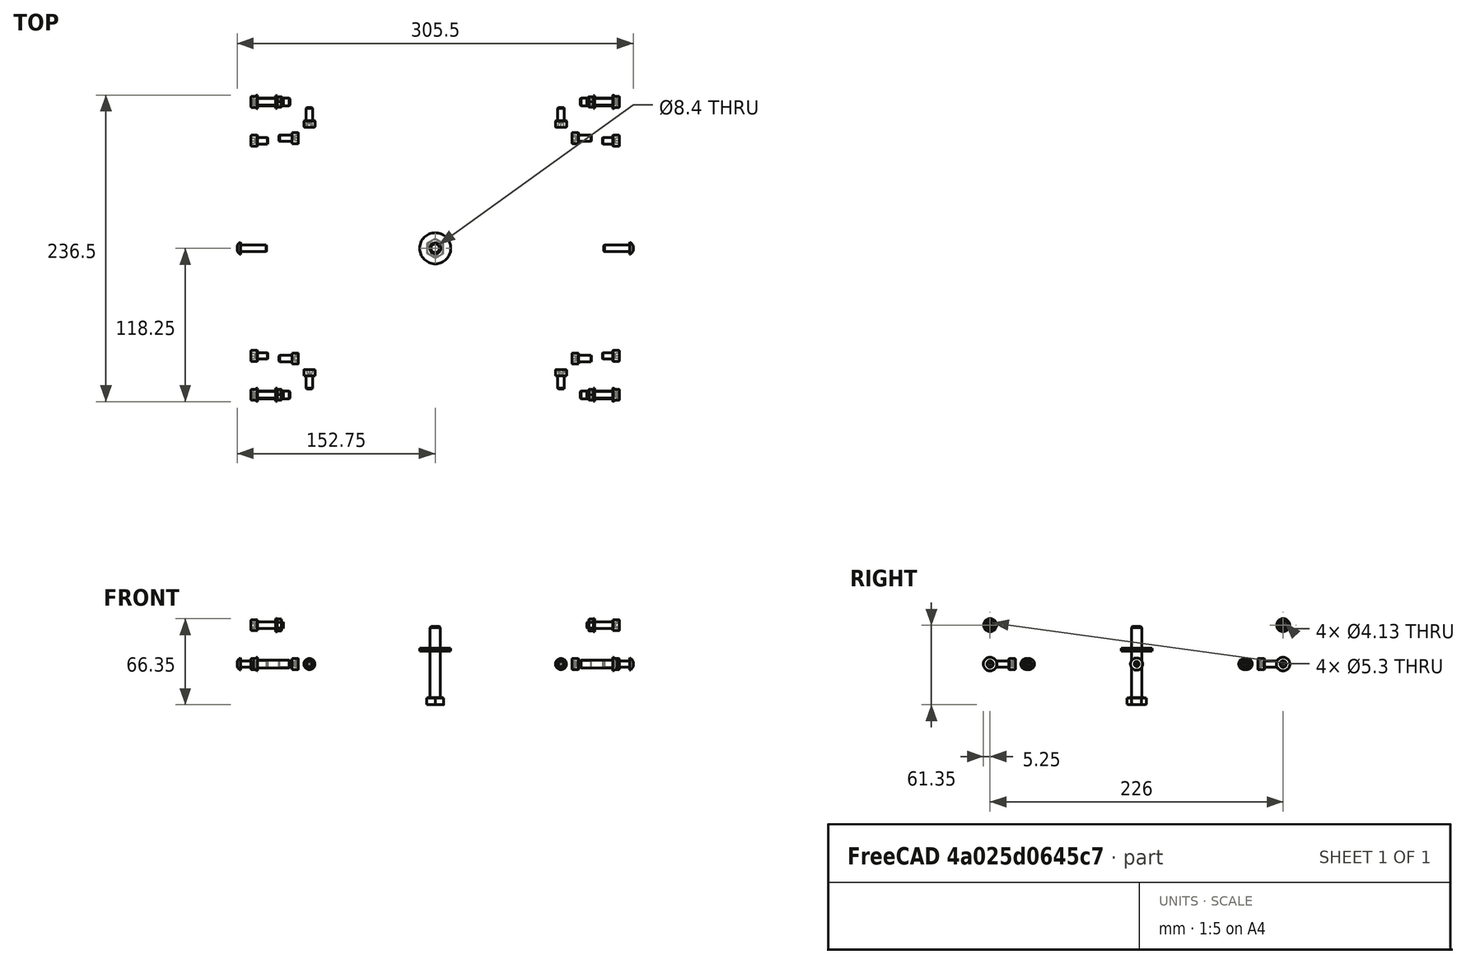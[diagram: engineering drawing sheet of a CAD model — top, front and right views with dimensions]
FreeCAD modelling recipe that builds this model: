
FCSTD DOCUMENT  (FreeCAD 0.19R24276 (Git))
Label: v5.6_Base
License: All rights reserved
LicenseURL: http://en.wikipedia.org/wiki/All_rights_reserved
objects: App::Link×37, Part::FeaturePython×32, App::DocumentObjectGroup×2, PartDesign::CoordinateSystem×2, App::FeaturePython×1, App::Part×1
note: 34 computed .brp shape members not serialized (recipe doc carries the construction recipe); baked Part::Feature solids carry a one-line shape summary decoded from their .brp
EXTERNAL_REF file=v5.6_Master.FCStd obj=LCS_AFrame_BaseHub
EXTERNAL_REF file=v5.6_Master.FCStd obj=Part002
EXTERNAL_REF file=v5.6_Master.FCStd obj=LCS_AFrame_Corner_AP
EXTERNAL_REF file=v5.6_Master.FCStd obj=Local_CS097
EXTERNAL_REF file=v5.6_Master.FCStd obj=Body038
EXTERNAL_REF file=v5.6_Master.FCStd obj=LCS_AFrame_Corner_FP
EXTERNAL_REF file=v5.6_Master.FCStd obj=LCS_AFrame_Corner_AS
EXTERNAL_REF file=v5.6_Master.FCStd obj=LCS_AFrame_Corner_FS
EXTERNAL_REF file=v5.6_Master.FCStd obj=LCS_AFrame_Post_AP
EXTERNAL_REF file=v5.6_Master.FCStd obj=Local_CS042
EXTERNAL_REF file=v5.6_Master.FCStd obj=Body018
EXTERNAL_REF file=v5.6_Master.FCStd obj=LCS_AFrame_Post_FP
EXTERNAL_REF file=v5.6_Master.FCStd obj=Local_CS044
EXTERNAL_REF file=v5.6_Master.FCStd obj=LCS_AFrame_Post_AS
EXTERNAL_REF file=v5.6_Master.FCStd obj=LCS_AFrame_Post_FS
EXTERNAL_REF file=v5.6_Master.FCStd obj=Local_CS208
EXTERNAL_REF file=v5.6_Master.FCStd obj=Body022020
EXTERNAL_REF file=v5.6_Master.FCStd obj=Local_CS061
EXTERNAL_REF file=v5.6_Master.FCStd obj=Body020
EXTERNAL_REF file=v5.6_Master.FCStd obj=Local_CS059
EXTERNAL_REF file=v5.6_Master.FCStd obj=Local_CS212
EXTERNAL_REF file=v5.6_Master.FCStd obj=Local_CS217
EXTERNAL_REF file=v5.6_Master.FCStd obj=Body022016
EXTERNAL_REF file=v5.6_Master.FCStd obj=Local_CS213
EXTERNAL_REF file=v5.6_Master.FCStd obj=Local_CS215
EXTERNAL_REF file=v5.6_Master.FCStd obj=Body022017
EXTERNAL_REF file=v5.6_Master.FCStd obj=Local_CS214
EXTERNAL_REF file=v5.6_Master.FCStd obj=Local_CS216
EXTERNAL_REF file=v5.6_Master.FCStd obj=Body022022
EXTERNAL_REF file=v5.6_Master.FCStd obj=Local_CS100
EXTERNAL_REF file=v5.6_Master.FCStd obj=Local_CS108
EXTERNAL_REF file=v5.6_Master.FCStd obj=Body039
EXTERNAL_REF file=v5.6_Master.FCStd obj=Local_CS109
EXTERNAL_REF file=v5.6_Master.FCStd obj=Local_CS111
EXTERNAL_REF file=v5.6_Master.FCStd obj=Local_CS113
EXTERNAL_REF file=v5.6_Master.FCStd obj=Local_CS110
EXTERNAL_REF file=v5.6_Master.FCStd obj=Local_CS112
EXTERNAL_REF file=v5.6_Master.FCStd obj=Local_CS207
EXTERNAL_REF file=v5.6_Master.FCStd obj=Local_CS098
EXTERNAL_REF file=v5.6_Master.FCStd obj=Local_CS099
EXTERNAL_REF file=v5.6_Master.FCStd obj=Local_CS063
EXTERNAL_REF file=v5.6_Master.FCStd obj=Local_CS065
EXTERNAL_REF file=v5.6_Master.FCStd obj=Local_CS182
EXTERNAL_REF file=v5.6_Master.FCStd obj=Local_CS184
EXTERNAL_REF file=v5.6_Master.FCStd obj=Local_CS183
EXTERNAL_REF file=v5.6_Master.FCStd obj=Local_CS185
EXTERNAL_REF file=v5.6_Master.FCStd obj=Local_CS189
EXTERNAL_REF file=v5.6_Master.FCStd obj=Local_CS190
EXTERNAL_REF file=v5.6_Master.FCStd obj=LCS_AFrame_Pivot
EXTERNAL_REF file=v5.6_Master.FCStd obj=Local_CS233
EXTERNAL_REF file=v5.6_Master.FCStd obj=Body022031
EXTERNAL_REF file=v5.6_Master.FCStd obj=Local_CS236
EXTERNAL_REF file=v5.6_Master.FCStd obj=Body003

FEATURE [App::DocumentObjectGroup] Parts
FEATURE [PartDesign::CoordinateSystem] LCS_Origin
  AttacherType = Attacher::AttachEngine3D
  MapMode = 2
  Support = -> [X_Axis]
FEATURE [App::DocumentObjectGroup] Constraints
FEATURE [App::FeaturePython] Variables  # WARN: FeaturePython — macro-defined, semantics opaque (R4)
FEATURE [App::Link] AziFrame
  AssemblyType = Asm4EE
  AttachedBy = #LCS_AFrame_BaseHub
  AttachedTo = Parent Assembly#LCS_Origin
  LinkedObject = -> <external v5.6_Master.FCStd>#Part002
  expr: Placement = LCS_Origin.Placement * AttachmentOffset * v5_6_Master#LCS_AFrame_BaseHub.Placement ^ -1
FEATURE [App::Link] AFrame_Bracket_AP
  AssemblyType = Asm4EE
  AttachedBy = #Local_CS097
  AttachedTo = AziFrame#LCS_AFrame_Corner_AP
  AttachmentOffset = pos=(0,0,0) rot=(0,0,1;3.14159rad)
  LinkPlacement = pos=(115,103,-4e-16) rot=(0,0,1;3.14159rad)
  LinkedObject = -> <external v5.6_Master.FCStd>#Body038
  Placement = pos=(115,103,-4e-16) rot=(0,0,1;3.14159rad)
  expr: Placement = AziFrame.Placement * v5_6_Master#LCS_AFrame_Corner_AP.Placement * AttachmentOffset * v5_6_Master#Local_CS097.Placement ^ -1
FEATURE [App::Link] AFrame_Bracket_FP
  AssemblyType = Asm4EE
  AttachedBy = #Local_CS097
  AttachedTo = AziFrame#LCS_AFrame_Corner_FP
  AttachmentOffset = pos=(0,0,0) rot=(0,0,1;1.5708rad)
  LinkPlacement = pos=(115,-103,-4e-16) rot=(0,0,1;1.5708rad)
  LinkedObject = -> <external v5.6_Master.FCStd>#Body038
  Placement = pos=(115,-103,-4e-16) rot=(0,0,1;1.5708rad)
  expr: Placement = AziFrame.Placement * v5_6_Master#LCS_AFrame_Corner_FP.Placement * AttachmentOffset * v5_6_Master#Local_CS097.Placement ^ -1
FEATURE [App::Link] AFrame_Bracket_AS
  AssemblyType = Asm4EE
  AttachedBy = #Local_CS097
  AttachedTo = AziFrame#LCS_AFrame_Corner_AS
  AttachmentOffset = pos=(0,0,0) rot=(0,0,1;4.71239rad)
  LinkPlacement = pos=(-115,103,-4e-16) rot=(0,0,1;4.71239rad)
  LinkedObject = -> <external v5.6_Master.FCStd>#Body038
  Placement = pos=(-115,103,-4e-16) rot=(0,0,1;4.71239rad)
  expr: Placement = AziFrame.Placement * v5_6_Master#LCS_AFrame_Corner_AS.Placement * AttachmentOffset * v5_6_Master#Local_CS097.Placement ^ -1
FEATURE [App::Link] AFrame_Bracket_FS
  AssemblyType = Asm4EE
  AttachedBy = #Local_CS097
  AttachedTo = AziFrame#LCS_AFrame_Corner_FS
  LinkPlacement = pos=(-115,-103,-4e-16) rot=(0,0,1;0rad)
  LinkedObject = -> <external v5.6_Master.FCStd>#Body038
  Placement = pos=(-115,-103,-4e-16) rot=(0,0,1;0rad)
  expr: Placement = AziFrame.Placement * v5_6_Master#LCS_AFrame_Corner_FS.Placement * AttachmentOffset * v5_6_Master#Local_CS097.Placement ^ -1
FEATURE [App::Link] RockerPost_AP
  AssemblyType = Asm4EE
  AttachedBy = #Local_CS042
  AttachedTo = AziFrame#LCS_AFrame_Post_AP
  AttachmentOffset = pos=(0,0,0) rot=(0.707107,-0.707107,0;3.14159rad)
  LinkPlacement = pos=(128,113,5) rot=(0,0,1;0rad)
  LinkedObject = -> <external v5.6_Master.FCStd>#Body018
  Placement = pos=(128,113,5) rot=(0,0,1;0rad)
  expr: Placement = AziFrame.Placement * v5_6_Master#LCS_AFrame_Post_AP.Placement * AttachmentOffset * v5_6_Master#Local_CS042.Placement ^ -1
FEATURE [App::Link] RockerPost_FP
  AssemblyType = Asm4EE
  AttachedBy = #Local_CS044
  AttachedTo = AziFrame#LCS_AFrame_Post_FP
  AttachmentOffset = pos=(0,0,0) rot=(-0.707107,-0.707107,0;3.14159rad)
  LinkPlacement = pos=(130,-113,5) rot=(0,0,-1;3.14159rad)
  LinkedObject = -> <external v5.6_Master.FCStd>#Body018
  Placement = pos=(130,-113,5) rot=(0,0,-1;3.14159rad)
  expr: Placement = AziFrame.Placement * v5_6_Master#LCS_AFrame_Post_FP.Placement * AttachmentOffset * v5_6_Master#Local_CS044.Placement ^ -1
FEATURE [App::Link] RockerPost_AS
  AssemblyType = Asm4EE
  AttachedBy = #Local_CS044
  AttachedTo = AziFrame#LCS_AFrame_Post_AS
  AttachmentOffset = pos=(0,0,0) rot=(-0.707107,-0.707107,0;3.14159rad)
  LinkPlacement = pos=(-130,113,5) rot=(0,0,1;0rad)
  LinkedObject = -> <external v5.6_Master.FCStd>#Body018
  Placement = pos=(-130,113,5) rot=(0,0,1;0rad)
  expr: Placement = AziFrame.Placement * v5_6_Master#LCS_AFrame_Post_AS.Placement * AttachmentOffset * v5_6_Master#Local_CS044.Placement ^ -1
FEATURE [App::Link] RockerPost_FS
  AssemblyType = Asm4EE
  AttachedBy = #Local_CS042
  AttachedTo = AziFrame#LCS_AFrame_Post_FS
  AttachmentOffset = pos=(0,0,0) rot=(0.707107,-0.707107,0;3.14159rad)
  LinkPlacement = pos=(-128,-113,5) rot=(0,0,1;3.14159rad)
  LinkedObject = -> <external v5.6_Master.FCStd>#Body018
  Placement = pos=(-128,-113,5) rot=(0,0,1;3.14159rad)
  expr: Placement = AziFrame.Placement * v5_6_Master#LCS_AFrame_Post_FS.Placement * AttachmentOffset * v5_6_Master#Local_CS042.Placement ^ -1
FEATURE [App::Link] AzimuthBase
  AssemblyType = Asm4EE
  AttachedBy = #Local_CS208
  AttachedTo = AziFrame#LCS_AFrame_BaseHub
  AttachmentOffset = pos=(0,0,-15) rot=(0,0,1;0rad)
  LinkPlacement = pos=(0,0,-15) rot=(0,0,1;1.5708rad)
  LinkedObject = -> <external v5.6_Master.FCStd>#Body022020
  Placement = pos=(0,0,-15) rot=(0,0,1;1.5708rad)
  expr: Placement = AziFrame.Placement * v5_6_Master#LCS_AFrame_BaseHub.Placement * AttachmentOffset * v5_6_Master#Local_CS208.Placement ^ -1
FEATURE [App::Link] SidePlate_P
  AssemblyType = Asm4EE
  AttachedBy = #Local_CS061
  AttachedTo = RockerPost_AP#Local_CS044
  AttachmentOffset = pos=(0,0,0) rot=(1,0,0;3.14159rad)
  LinkPlacement = pos=(135,-5.68e-14,5) rot=(0,0,1;0rad)
  LinkedObject = -> <external v5.6_Master.FCStd>#Body020
  Placement = pos=(135,-5.68e-14,5) rot=(0,0,1;0rad)
  expr: Placement = RockerPost_AP.Placement * v5_6_Master#Local_CS044.Placement * AttachmentOffset * v5_6_Master#Local_CS061.Placement ^ -1
FEATURE [App::Link] SidePlate_S
  AssemblyType = Asm4EE
  AttachedBy = #Local_CS059
  AttachedTo = RockerPost_AS#Local_CS042
  AttachmentOffset = pos=(0,0,0) rot=(0,1,0;3.14159rad)
  LinkPlacement = pos=(-137,0,5) rot=(0,0,1;0rad)
  LinkedObject = -> <external v5.6_Master.FCStd>#Body020
  Placement = pos=(-137,0,5) rot=(0,0,1;0rad)
  expr: Placement = RockerPost_AS.Placement * v5_6_Master#Local_CS042.Placement * AttachmentOffset * v5_6_Master#Local_CS059.Placement ^ -1
FEATURE [App::Link] ArmSpacer_P
  AssemblyType = Asm4EE
  AttachedBy = #Local_CS212
  AttachedTo = SidePlate_P#Local_CS217
  AttachmentOffset = pos=(0,0,1) rot=(0,0,1;0rad)
  LinkPlacement = pos=(137,-5.98e-14,3.91e-14) rot=(0,0,1;0rad)
  LinkedObject = -> <external v5.6_Master.FCStd>#Body022016
  Placement = pos=(137,-5.98e-14,3.91e-14) rot=(0,0,1;0rad)
  expr: Placement = SidePlate_P.Placement * v5_6_Master#Local_CS217.Placement * AttachmentOffset * v5_6_Master#Local_CS212.Placement ^ -1
FEATURE [App::Link] ArmSpacer_S
  AssemblyType = Asm4EE
  AttachedBy = #Local_CS212
  AttachedTo = SidePlate_S#Local_CS217
  AttachmentOffset = pos=(0,0,-1) rot=(1,0,0;3.14159rad)
  LinkPlacement = pos=(-137,-2.1e-15,-2.96e-14) rot=(0,0,1;3.14159rad)
  LinkedObject = -> <external v5.6_Master.FCStd>#Body022016
  Placement = pos=(-137,-2.1e-15,-2.96e-14) rot=(0,0,1;3.14159rad)
  expr: Placement = SidePlate_S.Placement * v5_6_Master#Local_CS217.Placement * AttachmentOffset * v5_6_Master#Local_CS212.Placement ^ -1
FEATURE [App::Link] ArmPost_P
  AssemblyType = Asm4EE
  AttachedBy = #Local_CS215
  AttachedTo = ArmSpacer_P#Local_CS213
  AttachmentOffset = pos=(0,0,10) rot=(0,0,1;0rad)
  LinkPlacement = pos=(158,-7.99e-14,-10) rot=(0,0,-1;3.14159rad)
  LinkedObject = -> <external v5.6_Master.FCStd>#Body022017
  Placement = pos=(158,-7.99e-14,-10) rot=(0,0,-1;3.14159rad)
  expr: Placement = ArmSpacer_P.Placement * v5_6_Master#Local_CS213.Placement * AttachmentOffset * v5_6_Master#Local_CS215.Placement ^ -1
FEATURE [App::Link] ArmPost_S
  AssemblyType = Asm4EE
  AttachedBy = #Local_CS215
  AttachedTo = ArmSpacer_S#Local_CS213
  AttachmentOffset = pos=(0,0,10) rot=(0,0,1;0rad)
  LinkPlacement = pos=(-158,6.1e-15,-10) rot=(0,0,1;0rad)
  LinkedObject = -> <external v5.6_Master.FCStd>#Body022017
  Placement = pos=(-158,6.1e-15,-10) rot=(0,0,1;0rad)
  expr: Placement = ArmSpacer_S.Placement * v5_6_Master#Local_CS213.Placement * AttachmentOffset * v5_6_Master#Local_CS215.Placement ^ -1
FEATURE [App::Link] ArmBrake_P
  AssemblyType = Asm4EE
  AttachedBy = #Local_CS216
  AttachedTo = ArmPost_P#Local_CS214
  AttachmentOffset = pos=(0,0,18) rot=(0,0,1;0rad)
  LinkPlacement = pos=(159,-2.78e-14,50) rot=(0,0,1;0rad)
  LinkedObject = -> <external v5.6_Master.FCStd>#Body022022
  Placement = pos=(159,-2.78e-14,50) rot=(0,0,1;0rad)
  expr: Placement = ArmPost_P.Placement * v5_6_Master#Local_CS214.Placement * AttachmentOffset * v5_6_Master#Local_CS216.Placement ^ -1
FEATURE [App::Link] ArmBrake_S
  AssemblyType = Asm4EE
  AttachedBy = #Local_CS216
  AttachedTo = ArmPost_S#Local_CS214
  AttachmentOffset = pos=(0,0,18) rot=(0,0,1;0rad)
  LinkPlacement = pos=(-159,1.49e-14,50) rot=(0,0,1;3.14159rad)
  LinkedObject = -> <external v5.6_Master.FCStd>#Body022022
  Placement = pos=(-159,1.49e-14,50) rot=(0,0,1;3.14159rad)
  expr: Placement = ArmPost_S.Placement * v5_6_Master#Local_CS214.Placement * AttachmentOffset * v5_6_Master#Local_CS216.Placement ^ -1
FEATURE [App::Link] AFBracket_AP_TNut_P
  AssemblyType = Asm4EE
  AttachedBy = #Local_CS100
  AttachedTo = AFrame_Bracket_AP#Local_CS108
  LinkPlacement = pos=(116.2,85,1.7e-15) rot=(-0.57735,-0.57735,0.57735;2.0944rad)
  LinkedObject = -> <external v5.6_Master.FCStd>#Body039
  Placement = pos=(116.2,85,1.7e-15) rot=(-0.57735,-0.57735,0.57735;2.0944rad)
  expr: Placement = AFrame_Bracket_AP.Placement * v5_6_Master#Local_CS108.Placement * AttachmentOffset * v5_6_Master#Local_CS100.Placement ^ -1
FEATURE [App::Link] AFBracket_AP_TNut_A
  AssemblyType = Asm4EE
  AttachedBy = #Local_CS100
  AttachedTo = AFrame_Bracket_AP#Local_CS109
  LinkPlacement = pos=(97,104.2,1.5e-15) rot=(0,-0.707107,0.707107;3.14159rad)
  LinkedObject = -> <external v5.6_Master.FCStd>#Body039
  Placement = pos=(97,104.2,1.5e-15) rot=(0,-0.707107,0.707107;3.14159rad)
  expr: Placement = AFrame_Bracket_AP.Placement * v5_6_Master#Local_CS109.Placement * AttachmentOffset * v5_6_Master#Local_CS100.Placement ^ -1
FEATURE [App::Link] AFBracket_FP_TNut_P
  AssemblyType = Asm4EE
  AttachedBy = #Local_CS100
  AttachedTo = AFrame_Bracket_FP#Local_CS109
  LinkPlacement = pos=(116.2,-85,1.4e-15) rot=(-0.57735,-0.57735,0.57735;2.0944rad)
  LinkedObject = -> <external v5.6_Master.FCStd>#Body039
  Placement = pos=(116.2,-85,1.4e-15) rot=(-0.57735,-0.57735,0.57735;2.0944rad)
  expr: Placement = AFrame_Bracket_FP.Placement * v5_6_Master#Local_CS109.Placement * AttachmentOffset * v5_6_Master#Local_CS100.Placement ^ -1
FEATURE [App::Link] AFBracket_FP_TNut_F
  AssemblyType = Asm4EE
  AttachedBy = #Local_CS100
  AttachedTo = AFrame_Bracket_FP#Local_CS108
  LinkPlacement = pos=(97,-104.2,1.6e-15) rot=(-1,0,0;1.5708rad)
  LinkedObject = -> <external v5.6_Master.FCStd>#Body039
  Placement = pos=(97,-104.2,1.6e-15) rot=(-1,0,0;1.5708rad)
  expr: Placement = AFrame_Bracket_FP.Placement * v5_6_Master#Local_CS108.Placement * AttachmentOffset * v5_6_Master#Local_CS100.Placement ^ -1
FEATURE [App::Link] AFBracket_AS_TNut_S
  AssemblyType = Asm4EE
  AttachedBy = #Local_CS100
  AttachedTo = AFrame_Bracket_AS#Local_CS109
  LinkPlacement = pos=(-116.2,85,1.3e-15) rot=(0.57735,-0.57735,0.57735;4.18879rad)
  LinkedObject = -> <external v5.6_Master.FCStd>#Body039
  Placement = pos=(-116.2,85,1.3e-15) rot=(0.57735,-0.57735,0.57735;4.18879rad)
  expr: Placement = AFrame_Bracket_AS.Placement * v5_6_Master#Local_CS109.Placement * AttachmentOffset * v5_6_Master#Local_CS100.Placement ^ -1
FEATURE [App::Link] AFBracket_AS_TNut_A
  AssemblyType = Asm4EE
  AttachedBy = #Local_CS100
  AttachedTo = AFrame_Bracket_AS#Local_CS108
  LinkPlacement = pos=(-97,104.2,1.6e-15) rot=(0,-0.707107,0.707107;3.14159rad)
  LinkedObject = -> <external v5.6_Master.FCStd>#Body039
  Placement = pos=(-97,104.2,1.6e-15) rot=(0,-0.707107,0.707107;3.14159rad)
  expr: Placement = AFrame_Bracket_AS.Placement * v5_6_Master#Local_CS108.Placement * AttachmentOffset * v5_6_Master#Local_CS100.Placement ^ -1
FEATURE [App::Link] AFBracket_FS_TNut_S
  AssemblyType = Asm4EE
  AttachedBy = #Local_CS100
  AttachedTo = AFrame_Bracket_FS#Local_CS108
  LinkPlacement = pos=(-116.2,-85,1.8e-15) rot=(-0.57735,0.57735,-0.57735;2.0944rad)
  LinkedObject = -> <external v5.6_Master.FCStd>#Body039
  Placement = pos=(-116.2,-85,1.8e-15) rot=(-0.57735,0.57735,-0.57735;2.0944rad)
  expr: Placement = AFrame_Bracket_FS.Placement * v5_6_Master#Local_CS108.Placement * AttachmentOffset * v5_6_Master#Local_CS100.Placement ^ -1
FEATURE [App::Link] AFBracket_FS_TNut_A
  AssemblyType = Asm4EE
  AttachedBy = #Local_CS100
  AttachedTo = AFrame_Bracket_FS#Local_CS109
  LinkPlacement = pos=(-97,-104.2,1.5e-15) rot=(-1,0,0;1.5708rad)
  LinkedObject = -> <external v5.6_Master.FCStd>#Body039
  Placement = pos=(-97,-104.2,1.5e-15) rot=(-1,0,0;1.5708rad)
  expr: Placement = AFrame_Bracket_FS.Placement * v5_6_Master#Local_CS109.Placement * AttachmentOffset * v5_6_Master#Local_CS100.Placement ^ -1
FEATURE [App::Link] SidePlate_P_TNut_A
  AssemblyType = Asm4EE
  AttachedBy = #Local_CS100
  AttachedTo = SidePlate_P#Local_CS111
  AttachmentOffset = pos=(0,0,0) rot=(0.707107,-0.707107,0;3.14159rad)
  LinkPlacement = pos=(133.8,83,1.41e-14) rot=(0.57735,0.57735,0.57735;2.0944rad)
  LinkedObject = -> <external v5.6_Master.FCStd>#Body039
  Placement = pos=(133.8,83,1.41e-14) rot=(0.57735,0.57735,0.57735;2.0944rad)
  expr: Placement = SidePlate_P.Placement * v5_6_Master#Local_CS111.Placement * AttachmentOffset * v5_6_Master#Local_CS100.Placement ^ -1
FEATURE [App::Link] SidePlate_P_TNut_F
  AssemblyType = Asm4EE
  AttachedBy = #Local_CS100
  AttachedTo = SidePlate_P#Local_CS113
  AttachmentOffset = pos=(0,0,0) rot=(0.707107,-0.707107,0;3.14159rad)
  LinkPlacement = pos=(133.8,-83,6.56e-14) rot=(0.57735,0.57735,0.57735;2.0944rad)
  LinkedObject = -> <external v5.6_Master.FCStd>#Body039
  Placement = pos=(133.8,-83,6.56e-14) rot=(0.57735,0.57735,0.57735;2.0944rad)
  expr: Placement = SidePlate_P.Placement * v5_6_Master#Local_CS113.Placement * AttachmentOffset * v5_6_Master#Local_CS100.Placement ^ -1
FEATURE [App::Link] SidePlate_S_TNut_A
  AssemblyType = Asm4EE
  AttachedBy = #Local_CS100
  AttachedTo = SidePlate_S#Local_CS110
  AttachmentOffset = pos=(0,0,0) rot=(0.707107,-0.707107,0;3.14159rad)
  LinkPlacement = pos=(-133.8,83,-5.16e-14) rot=(-0.57735,0.57735,0.57735;4.18879rad)
  LinkedObject = -> <external v5.6_Master.FCStd>#Body039
  Placement = pos=(-133.8,83,-5.16e-14) rot=(-0.57735,0.57735,0.57735;4.18879rad)
  expr: Placement = SidePlate_S.Placement * v5_6_Master#Local_CS110.Placement * AttachmentOffset * v5_6_Master#Local_CS100.Placement ^ -1
FEATURE [App::Link] SidePlate_S_TNut_F
  AssemblyType = Asm4EE
  AttachedBy = #Local_CS100
  AttachedTo = SidePlate_S#Local_CS112
  AttachmentOffset = pos=(0,0,0) rot=(0.707107,-0.707107,0;3.14159rad)
  LinkPlacement = pos=(-133.8,-83,-3.6e-15) rot=(-0.57735,0.57735,0.57735;4.18879rad)
  LinkedObject = -> <external v5.6_Master.FCStd>#Body039
  Placement = pos=(-133.8,-83,-3.6e-15) rot=(-0.57735,0.57735,0.57735;4.18879rad)
  expr: Placement = SidePlate_S.Placement * v5_6_Master#Local_CS112.Placement * AttachmentOffset * v5_6_Master#Local_CS100.Placement ^ -1
FEATURE [App::Link] SideBrake_P_TNut_N
  AssemblyType = Asm4EE
  AttachedBy = #Local_CS100
  AttachedTo = ArmSpacer_P#Local_CS212
  AttachmentOffset = pos=(0,0,0) rot=(0,0,1;1.5708rad)
  LinkPlacement = pos=(135.8,-5.92e-14,4.1e-14) rot=(-0.57735,-0.57735,-0.57735;4.18879rad)
  LinkedObject = -> <external v5.6_Master.FCStd>#Body039
  Placement = pos=(135.8,-5.92e-14,4.1e-14) rot=(-0.57735,-0.57735,-0.57735;4.18879rad)
  expr: Placement = ArmSpacer_P.Placement * v5_6_Master#Local_CS212.Placement * AttachmentOffset * v5_6_Master#Local_CS100.Placement ^ -1
FEATURE [App::Link] SideBrake_S_TNut_N
  AssemblyType = Asm4EE
  AttachedBy = #Local_CS100
  AttachedTo = ArmSpacer_S#Local_CS212
  AttachmentOffset = pos=(0,0,0) rot=(0,0,1;1.5708rad)
  LinkPlacement = pos=(-135.8,-2.6e-15,-2.76e-14) rot=(-0.57735,0.57735,0.57735;4.18879rad)
  LinkedObject = -> <external v5.6_Master.FCStd>#Body039
  Placement = pos=(-135.8,-2.6e-15,-2.76e-14) rot=(-0.57735,0.57735,0.57735;4.18879rad)
  expr: Placement = ArmSpacer_S.Placement * v5_6_Master#Local_CS212.Placement * AttachmentOffset * v5_6_Master#Local_CS100.Placement ^ -1
FEATURE [App::Link] SideBrake_P_TNut_Z
  AssemblyType = Asm4EE
  AttachedBy = #Local_CS100
  AttachedTo = ArmPost_P#Local_CS214
  AttachmentOffset = pos=(0,0,10) rot=(0,0,1;0rad)
  LinkPlacement = pos=(166.8,-3.12e-14,50) rot=(0,-1,0;4.71239rad)
  LinkedObject = -> <external v5.6_Master.FCStd>#Body039
  Placement = pos=(166.8,-3.12e-14,50) rot=(0,-1,0;4.71239rad)
  expr: Placement = ArmPost_P.Placement * v5_6_Master#Local_CS214.Placement * AttachmentOffset * v5_6_Master#Local_CS100.Placement ^ -1
FEATURE [App::Link] SideBrake_S_TNut_Z
  AssemblyType = Asm4EE
  AttachedBy = #Local_CS100
  AttachedTo = ArmPost_S#Local_CS214
  AttachmentOffset = pos=(0,0,10) rot=(0,0,1;0rad)
  LinkPlacement = pos=(-166.8,1.76e-14,50) rot=(-0.707107,0,0.707107;3.14159rad)
  LinkedObject = -> <external v5.6_Master.FCStd>#Body039
  Placement = pos=(-166.8,1.76e-14,50) rot=(-0.707107,0,0.707107;3.14159rad)
  expr: Placement = ArmPost_S.Placement * v5_6_Master#Local_CS214.Placement * AttachmentOffset * v5_6_Master#Local_CS100.Placement ^ -1
FEATURE [Part::FeaturePython] Screw  label="M8x55-Screw"  # Fasteners workbench fastener (typed FeaturePython)
  AssemblyType = Asm4EE
  AttachedBy = Origin
  AttachedTo = AzimuthBase#Local_CS207
  AttachmentOffset = pos=(0,0,0) rot=(0,0,1;1.5708rad)
  Placement = pos=(0,0,-26.05) rot=(0.707107,0.707107,0;3.14159rad)
  diameter = 9
  invert = false
  length = 5
  lengthCustom = 55
  matchOuter = false
  offset = 0
  thread = false
  type = 26
  expr: Placement = AzimuthBase.Placement * v5_6_Master#Local_CS207.Placement * AttachmentOffset
FEATURE [Part::FeaturePython] Washer  label="M8-Washer"  # Fasteners workbench fastener (typed FeaturePython)
  AssemblyType = Asm4EE
  AttachedBy = Origin
  AttachedTo = AziFrame#LCS_AFrame_BaseHub
  AttachmentOffset = pos=(0,0,10) rot=(0,0,1;0rad)
  Placement = pos=(0,0,10) rot=(0,0,1;0rad)
  diameter = 6
  invert = false
  matchOuter = false
  offset = 0
  type = 6
  expr: Placement = AziFrame.Placement * v5_6_Master#LCS_AFrame_BaseHub.Placement * AttachmentOffset
FEATURE [Part::FeaturePython] Screw001  label="M5x10-Screw"  # Fasteners workbench fastener (typed FeaturePython)
  AssemblyType = Asm4EE
  AttachedBy = Origin
  AttachedTo = AFrame_Bracket_AP#Local_CS098
  Placement = pos=(110.5,85,3.8e-15) rot=(-0.57735,0.57735,0.57735;4.18879rad)
  diameter = 6
  invert = false
  length = 1
  lengthCustom = 10
  matchOuter = false
  offset = 0
  thread = false
  type = 32
  expr: Placement = AFrame_Bracket_AP.Placement * v5_6_Master#Local_CS098.Placement * AttachmentOffset
FEATURE [Part::FeaturePython] Screw002  label="M5x10-Screw129"  # Fasteners workbench fastener (typed FeaturePython)
  AssemblyType = Asm4EE
  AttachedBy = Origin
  AttachedTo = AFrame_Bracket_AP#Local_CS099
  Placement = pos=(97,98.5,3.3e-15) rot=(-0.57735,-0.57735,0.57735;4.18879rad)
  diameter = 6
  invert = false
  length = 1
  lengthCustom = 10
  matchOuter = false
  offset = 0
  thread = false
  type = 32
  expr: Placement = AFrame_Bracket_AP.Placement * v5_6_Master#Local_CS099.Placement * AttachmentOffset
FEATURE [Part::FeaturePython] Screw003  label="M5x10-Screw130"  # Fasteners workbench fastener (typed FeaturePython)
  AssemblyType = Asm4EE
  AttachedBy = Origin
  AttachedTo = AFrame_Bracket_FP#Local_CS098
  Placement = pos=(97,-98.5,3.8e-15) rot=(0,0.707107,0.707107;3.14159rad)
  diameter = 6
  invert = false
  length = 1
  lengthCustom = 10
  matchOuter = false
  offset = 0
  thread = false
  type = 32
  expr: Placement = AFrame_Bracket_FP.Placement * v5_6_Master#Local_CS098.Placement * AttachmentOffset
FEATURE [Part::FeaturePython] Screw004  label="M5x10-Screw131"  # Fasteners workbench fastener (typed FeaturePython)
  AssemblyType = Asm4EE
  AttachedBy = Origin
  AttachedTo = AFrame_Bracket_FP#Local_CS099
  Placement = pos=(110.5,-85,3.3e-15) rot=(-0.707107,0,0.707107;3.14159rad)
  diameter = 6
  invert = false
  length = 1
  lengthCustom = 10
  matchOuter = false
  offset = 0
  thread = false
  type = 32
  expr: Placement = AFrame_Bracket_FP.Placement * v5_6_Master#Local_CS099.Placement * AttachmentOffset
FEATURE [Part::FeaturePython] Screw005  label="M5x10-Screw132"  # Fasteners workbench fastener (typed FeaturePython)
  AssemblyType = Asm4EE
  AttachedBy = Origin
  AttachedTo = AFrame_Bracket_AS#Local_CS098
  Placement = pos=(-97,98.5,3.8e-15) rot=(-1,0,0;4.71239rad)
  diameter = 6
  invert = false
  length = 1
  lengthCustom = 10
  matchOuter = false
  offset = 0
  thread = false
  type = 32
  expr: Placement = AFrame_Bracket_AS.Placement * v5_6_Master#Local_CS098.Placement * AttachmentOffset
FEATURE [Part::FeaturePython] Screw006  label="M5x10-Screw133"  # Fasteners workbench fastener (typed FeaturePython)
  AssemblyType = Asm4EE
  AttachedBy = Origin
  AttachedTo = AFrame_Bracket_AS#Local_CS099
  Placement = pos=(-110.5,85,3.3e-15) rot=(0,-1,0;4.71239rad)
  diameter = 6
  invert = false
  length = 1
  lengthCustom = 10
  matchOuter = false
  offset = 0
  thread = false
  type = 32
  expr: Placement = AFrame_Bracket_AS.Placement * v5_6_Master#Local_CS099.Placement * AttachmentOffset
FEATURE [Part::FeaturePython] Screw007  label="M5x10-Screw134"  # Fasteners workbench fastener (typed FeaturePython)
  AssemblyType = Asm4EE
  AttachedBy = Origin
  AttachedTo = AFrame_Bracket_FS#Local_CS098
  Placement = pos=(-110.5,-85,3.8e-15) rot=(0.57735,0.57735,0.57735;2.0944rad)
  diameter = 6
  invert = false
  length = 1
  lengthCustom = 10
  matchOuter = false
  offset = 0
  thread = false
  type = 32
  expr: Placement = AFrame_Bracket_FS.Placement * v5_6_Master#Local_CS098.Placement * AttachmentOffset
FEATURE [Part::FeaturePython] Screw008  label="M5x10-Screw135"  # Fasteners workbench fastener (typed FeaturePython)
  AssemblyType = Asm4EE
  AttachedBy = Origin
  AttachedTo = AFrame_Bracket_FS#Local_CS099
  Placement = pos=(-97,-98.5,3.3e-15) rot=(-0.57735,0.57735,0.57735;2.0944rad)
  diameter = 6
  invert = false
  length = 1
  lengthCustom = 10
  matchOuter = false
  offset = 0
  thread = false
  type = 32
  expr: Placement = AFrame_Bracket_FS.Placement * v5_6_Master#Local_CS099.Placement * AttachmentOffset
FEATURE [Part::FeaturePython] Screw009  label="M6x25-Screw"  # Fasteners workbench fastener (typed FeaturePython)
  AssemblyType = Asm4EE
  AttachedBy = Origin
  AttachedTo = SidePlate_P#Local_CS059
  Placement = pos=(137,113,4.4e-15) rot=(-0.707107,0,-0.707107;3.14159rad)
  diameter = 4
  invert = false
  length = 5
  lengthCustom = 25
  matchOuter = false
  offset = 0
  thread = false
  type = 38
  expr: Placement = SidePlate_P.Placement * v5_6_Master#Local_CS059.Placement * AttachmentOffset
FEATURE [Part::FeaturePython] Screw010  label="M6x25-Screw040"  # Fasteners workbench fastener (typed FeaturePython)
  AssemblyType = Asm4EE
  AttachedBy = Origin
  AttachedTo = SidePlate_P#Local_CS063
  Placement = pos=(137,-113,7.55e-14) rot=(-0.707107,0,-0.707107;3.14159rad)
  diameter = 4
  invert = false
  length = 5
  lengthCustom = 25
  matchOuter = false
  offset = 0
  thread = false
  type = 38
  expr: Placement = SidePlate_P.Placement * v5_6_Master#Local_CS063.Placement * AttachmentOffset
FEATURE [Part::FeaturePython] Screw011  label="M6x25-Screw041"  # Fasteners workbench fastener (typed FeaturePython)
  AssemblyType = Asm4EE
  AttachedBy = Origin
  AttachedTo = SidePlate_S#Local_CS061
  Placement = pos=(-137,113,-6.22e-14) rot=(0,1,0;4.71239rad)
  diameter = 4
  invert = false
  length = 5
  lengthCustom = 25
  matchOuter = false
  offset = 0
  thread = false
  type = 38
  expr: Placement = SidePlate_S.Placement * v5_6_Master#Local_CS061.Placement * AttachmentOffset
FEATURE [Part::FeaturePython] Screw012  label="M6x25-Screw042"  # Fasteners workbench fastener (typed FeaturePython)
  AssemblyType = Asm4EE
  AttachedBy = Origin
  AttachedTo = SidePlate_S#Local_CS065
  Placement = pos=(-137,-113,3.6e-15) rot=(0,1,0;4.71239rad)
  diameter = 4
  invert = false
  length = 5
  lengthCustom = 25
  matchOuter = false
  offset = 0
  thread = false
  type = 38
  expr: Placement = SidePlate_S.Placement * v5_6_Master#Local_CS065.Placement * AttachmentOffset
FEATURE [Part::FeaturePython] Screw013  label="M5x8-Screw"  # Fasteners workbench fastener (typed FeaturePython)
  AssemblyType = Asm4EE
  AttachedBy = Origin
  AttachedTo = SidePlate_P#Local_CS110
  Placement = pos=(137,83,1.42e-14) rot=(-0.707107,0,-0.707107;3.14159rad)
  diameter = 6
  invert = false
  length = 0
  lengthCustom = 8
  matchOuter = false
  offset = 0
  thread = false
  type = 32
  expr: Placement = SidePlate_P.Placement * v5_6_Master#Local_CS110.Placement * AttachmentOffset
FEATURE [Part::FeaturePython] Screw014  label="M5x8-Screw049"  # Fasteners workbench fastener (typed FeaturePython)
  AssemblyType = Asm4EE
  AttachedBy = Origin
  AttachedTo = SidePlate_P#Local_CS112
  Placement = pos=(137,-83,6.57e-14) rot=(-0.707107,0,-0.707107;3.14159rad)
  diameter = 6
  invert = false
  length = 0
  lengthCustom = 8
  matchOuter = false
  offset = 0
  thread = false
  type = 32
  expr: Placement = SidePlate_P.Placement * v5_6_Master#Local_CS112.Placement * AttachmentOffset
FEATURE [Part::FeaturePython] Screw015  label="M5x8-Screw050"  # Fasteners workbench fastener (typed FeaturePython)
  AssemblyType = Asm4EE
  AttachedBy = Origin
  AttachedTo = SidePlate_S#Local_CS111
  Placement = pos=(-137,83,-5.33e-14) rot=(0,1,0;4.71239rad)
  diameter = 6
  invert = false
  length = 0
  lengthCustom = 8
  matchOuter = false
  offset = 0
  thread = false
  type = 32
  expr: Placement = SidePlate_S.Placement * v5_6_Master#Local_CS111.Placement * AttachmentOffset
FEATURE [Part::FeaturePython] Screw016  label="M5x8-Screw051"  # Fasteners workbench fastener (typed FeaturePython)
  AssemblyType = Asm4EE
  AttachedBy = Origin
  AttachedTo = SidePlate_S#Local_CS113
  Placement = pos=(-137,-83,-5.3e-15) rot=(0,1,0;4.71239rad)
  diameter = 6
  invert = false
  length = 0
  lengthCustom = 8
  matchOuter = false
  offset = 0
  thread = false
  type = 32
  expr: Placement = SidePlate_S.Placement * v5_6_Master#Local_CS113.Placement * AttachmentOffset
FEATURE [Part::FeaturePython] Screw017  label="M5x20-Screw"  # Fasteners workbench fastener (typed FeaturePython)
  AssemblyType = Asm4EE
  AttachedBy = Origin
  AttachedTo = SidePlate_P#Local_CS182
  Placement = pos=(137,113,30) rot=(-0.707107,0,-0.707107;3.14159rad)
  diameter = 6
  invert = false
  length = 5
  lengthCustom = 20
  matchOuter = false
  offset = 0
  thread = false
  type = 32
  expr: Placement = SidePlate_P.Placement * v5_6_Master#Local_CS182.Placement * AttachmentOffset
FEATURE [Part::FeaturePython] Screw018  label="M5x20-Screw087"  # Fasteners workbench fastener (typed FeaturePython)
  AssemblyType = Asm4EE
  AttachedBy = Origin
  AttachedTo = SidePlate_P#Local_CS184
  Placement = pos=(137,-113,30) rot=(-0.707107,0,-0.707107;3.14159rad)
  diameter = 6
  invert = false
  length = 5
  lengthCustom = 20
  matchOuter = false
  offset = 0
  thread = false
  type = 32
  expr: Placement = SidePlate_P.Placement * v5_6_Master#Local_CS184.Placement * AttachmentOffset
FEATURE [Part::FeaturePython] Screw019  label="M5x20-Screw088"  # Fasteners workbench fastener (typed FeaturePython)
  AssemblyType = Asm4EE
  AttachedBy = Origin
  AttachedTo = SidePlate_S#Local_CS183
  Placement = pos=(-137,113,30) rot=(0,1,0;4.71239rad)
  diameter = 6
  invert = false
  length = 5
  lengthCustom = 20
  matchOuter = false
  offset = 0
  thread = false
  type = 32
  expr: Placement = SidePlate_S.Placement * v5_6_Master#Local_CS183.Placement * AttachmentOffset
FEATURE [Part::FeaturePython] Screw020  label="M5x20-Screw089"  # Fasteners workbench fastener (typed FeaturePython)
  AssemblyType = Asm4EE
  AttachedBy = Origin
  AttachedTo = SidePlate_S#Local_CS185
  Placement = pos=(-137,-113,30) rot=(0,1,0;4.71239rad)
  diameter = 6
  invert = false
  length = 5
  lengthCustom = 20
  matchOuter = false
  offset = 0
  thread = false
  type = 32
  expr: Placement = SidePlate_S.Placement * v5_6_Master#Local_CS185.Placement * AttachmentOffset
FEATURE [Part::FeaturePython] Washer001  label="M5-Washer"  # Fasteners workbench fastener (typed FeaturePython)
  AssemblyType = Asm4EE
  AttachedBy = Origin
  AttachedTo = RockerPost_AP#Local_CS189
  Placement = pos=(123,113,30) rot=(0.707107,0,-0.707107;3.14159rad)
  diameter = 6
  invert = false
  matchOuter = false
  offset = 0
  type = 3
  expr: Placement = RockerPost_AP.Placement * v5_6_Master#Local_CS189.Placement * AttachmentOffset
FEATURE [Part::FeaturePython] Washer002  label="M5-Washer049"  # Fasteners workbench fastener (typed FeaturePython)
  AssemblyType = Asm4EE
  AttachedBy = Origin
  AttachedTo = RockerPost_FP#Local_CS190
  Placement = pos=(123,-113,30) rot=(0,-1,0;1.5708rad)
  diameter = 6
  invert = false
  matchOuter = false
  offset = 0
  type = 3
  expr: Placement = RockerPost_FP.Placement * v5_6_Master#Local_CS190.Placement * AttachmentOffset
FEATURE [Part::FeaturePython] Washer003  label="M5-Washer050"  # Fasteners workbench fastener (typed FeaturePython)
  AssemblyType = Asm4EE
  AttachedBy = Origin
  AttachedTo = RockerPost_AS#Local_CS190
  Placement = pos=(-123,113,30) rot=(0.707107,0,0.707107;3.14159rad)
  diameter = 6
  invert = false
  matchOuter = false
  offset = 0
  type = 3
  expr: Placement = RockerPost_AS.Placement * v5_6_Master#Local_CS190.Placement * AttachmentOffset
FEATURE [Part::FeaturePython] Washer004  label="M5-Washer051"  # Fasteners workbench fastener (typed FeaturePython)
  AssemblyType = Asm4EE
  AttachedBy = Origin
  AttachedTo = RockerPost_FS#Local_CS189
  Placement = pos=(-123,-113,30) rot=(0,1,0;1.5708rad)
  diameter = 6
  invert = false
  matchOuter = false
  offset = 0
  type = 3
  expr: Placement = RockerPost_FS.Placement * v5_6_Master#Local_CS189.Placement * AttachmentOffset
FEATURE [Part::FeaturePython] Nut001  label="M5-Nut"  # Fasteners workbench fastener (typed FeaturePython)
  AssemblyType = Asm4EE
  AttachedBy = Origin
  AttachedTo = RockerPost_AP#Local_CS189
  AttachmentOffset = pos=(0,0,1) rot=(0,0,1;0rad)
  Placement = pos=(122,113,30) rot=(0.707107,0,-0.707107;3.14159rad)
  diameter = 7
  invert = false
  matchOuter = false
  offset = 0
  thread = false
  type = 7
  expr: Placement = RockerPost_AP.Placement * v5_6_Master#Local_CS189.Placement * AttachmentOffset
FEATURE [Part::FeaturePython] Nut002  label="M5-Nut049"  # Fasteners workbench fastener (typed FeaturePython)
  AssemblyType = Asm4EE
  AttachedBy = Origin
  AttachedTo = RockerPost_FP#Local_CS190
  AttachmentOffset = pos=(0,0,1) rot=(0,0,1;0rad)
  Placement = pos=(122,-113,30) rot=(0,-1,0;1.5708rad)
  diameter = 7
  invert = false
  matchOuter = false
  offset = 0
  thread = false
  type = 7
  expr: Placement = RockerPost_FP.Placement * v5_6_Master#Local_CS190.Placement * AttachmentOffset
FEATURE [Part::FeaturePython] Nut003  label="M5-Nut050"  # Fasteners workbench fastener (typed FeaturePython)
  AssemblyType = Asm4EE
  AttachedBy = Origin
  AttachedTo = RockerPost_AS#Local_CS190
  AttachmentOffset = pos=(0,0,1) rot=(0,0,1;0rad)
  Placement = pos=(-122,113,30) rot=(0.707107,0,0.707107;3.14159rad)
  diameter = 7
  invert = false
  matchOuter = false
  offset = 0
  thread = false
  type = 7
  expr: Placement = RockerPost_AS.Placement * v5_6_Master#Local_CS190.Placement * AttachmentOffset
FEATURE [Part::FeaturePython] Nut004  label="M5-Nut051"  # Fasteners workbench fastener (typed FeaturePython)
  AssemblyType = Asm4EE
  AttachedBy = Origin
  AttachedTo = RockerPost_FS#Local_CS189
  AttachmentOffset = pos=(0,0,1) rot=(0,0,1;0rad)
  Placement = pos=(-122,-113,30) rot=(0,1,0;1.5708rad)
  diameter = 7
  invert = false
  matchOuter = false
  offset = 0
  thread = false
  type = 7
  expr: Placement = RockerPost_FS.Placement * v5_6_Master#Local_CS189.Placement * AttachmentOffset
FEATURE [Part::FeaturePython] Screw021  label="M5x20-Screw090"  # Fasteners workbench fastener (typed FeaturePython)
  AssemblyType = Asm4EE
  AttachedBy = Origin
  AttachedTo = ArmPost_P#Local_CS215
  AttachmentOffset = pos=(0,0,-8) rot=(0,0,1;0rad)
  Placement = pos=(150,-6.69e-14,4.17e-14) rot=(-0.707107,0,-0.707107;3.14159rad)
  diameter = 3
  invert = false
  length = 5
  lengthCustom = 20
  matchOuter = false
  offset = 0
  thread = false
  type = 38
  expr: Placement = ArmPost_P.Placement * v5_6_Master#Local_CS215.Placement * AttachmentOffset
FEATURE [Part::FeaturePython] Screw022  label="M5x20-Screw091"  # Fasteners workbench fastener (typed FeaturePython)
  AssemblyType = Asm4EE
  AttachedBy = Origin
  AttachedTo = ArmPost_S#Local_CS215
  AttachmentOffset = pos=(0,0,-8) rot=(0,0,1;0rad)
  Placement = pos=(-150,3.9e-15,-2.93e-14) rot=(0,1,0;4.71239rad)
  diameter = 3
  invert = false
  length = 5
  lengthCustom = 20
  matchOuter = false
  offset = 0
  thread = false
  type = 38
  expr: Placement = ArmPost_S.Placement * v5_6_Master#Local_CS215.Placement * AttachmentOffset
FEATURE [PartDesign::CoordinateSystem] LCS_BaseAssembly_Pivot
  AttacherType = Attacher::AttachEngine3D
  Placement = pos=(0,0,215) rot=(0,0,1;0rad)
  expr: Placement = AziFrame.Placement * v5_6_Master#LCS_AFrame_Pivot.Placement * AttachmentOffset
FEATURE [App::Link] BaseBolt
  AssemblyType = Asm4EE
  AttachedBy = #Local_CS233
  AttachedTo = AziFrame#LCS_AFrame_BaseHub
  AttachmentOffset = pos=(0,0,14) rot=(0,0,1;0rad)
  LinkPlacement = pos=(0,0,14) rot=(0,0,-1;1.5708rad)
  LinkedObject = -> <external v5.6_Master.FCStd>#Body022031
  Placement = pos=(0,0,14) rot=(0,0,-1;1.5708rad)
  expr: Placement = AziFrame.Placement * v5_6_Master#LCS_AFrame_BaseHub.Placement * AttachmentOffset * v5_6_Master#Local_CS233.Placement ^ -1
FEATURE [App::Link] SideArm_P_Knob
  AssemblyType = Asm4EE
  AttachedBy = #Local_CS236
  AttachedTo = ArmBrake_P#Local_CS216
  LinkPlacement = pos=(176,-3.53e-14,50) rot=(-0.57735,-0.57735,-0.57735;4.18879rad)
  LinkedObject = -> <external v5.6_Master.FCStd>#Body003
  Placement = pos=(176,-3.53e-14,50) rot=(-0.57735,-0.57735,-0.57735;4.18879rad)
  expr: Placement = ArmBrake_P.Placement * v5_6_Master#Local_CS216.Placement * AttachmentOffset * v5_6_Master#Local_CS236.Placement ^ -1
FEATURE [App::Link] SideArm_S_Knob
  AssemblyType = Asm4EE
  AttachedBy = #Local_CS236
  AttachedTo = ArmBrake_S#Local_CS216
  LinkPlacement = pos=(-176,2.09e-14,50) rot=(-0.57735,0.57735,0.57735;4.18879rad)
  LinkedObject = -> <external v5.6_Master.FCStd>#Body003
  Placement = pos=(-176,2.09e-14,50) rot=(-0.57735,0.57735,0.57735;4.18879rad)
  expr: Placement = ArmBrake_S.Placement * v5_6_Master#Local_CS216.Placement * AttachmentOffset * v5_6_Master#Local_CS236.Placement ^ -1
FEATURE [App::Part] Model  label="Base"
  Configuration = 0
  Group = -> [LCS_Origin,Constraints,Variables,AziFrame,AFrame_Bracket_AP,AFrame_Bracket_FP,AFrame_Bracket_AS,AFrame_Bracket_FS,RockerPost_AP,RockerPost_FP,RockerPost_AS,RockerPost_FS,AzimuthBase,SidePlate_P,SidePlate_S,ArmSpacer_P,ArmSpacer_S,ArmPost_P,ArmPost_S,ArmBrake_P,ArmBrake_S,AFBracket_AP_TNut_P,AFBracket_AP_TNut_A,AFBracket_FP_TNut_P,AFBracket_FP_TNut_F,AFBracket_AS_TNut_S,AFBracket_AS_TNut_A,+46 more]
  Origin = -> Origin
  Type = Assembly4 Model

RESOLVED EXTERNAL PARTS (link-assembly join: the EXTERNAL_REF files above that resolve inside this repo's crawl, each included once):
---- part v5.6_Master.FCStd = doc fcstd_204eddf974d0 (447149 chars; too large to inline — full recipe in that document) ----
